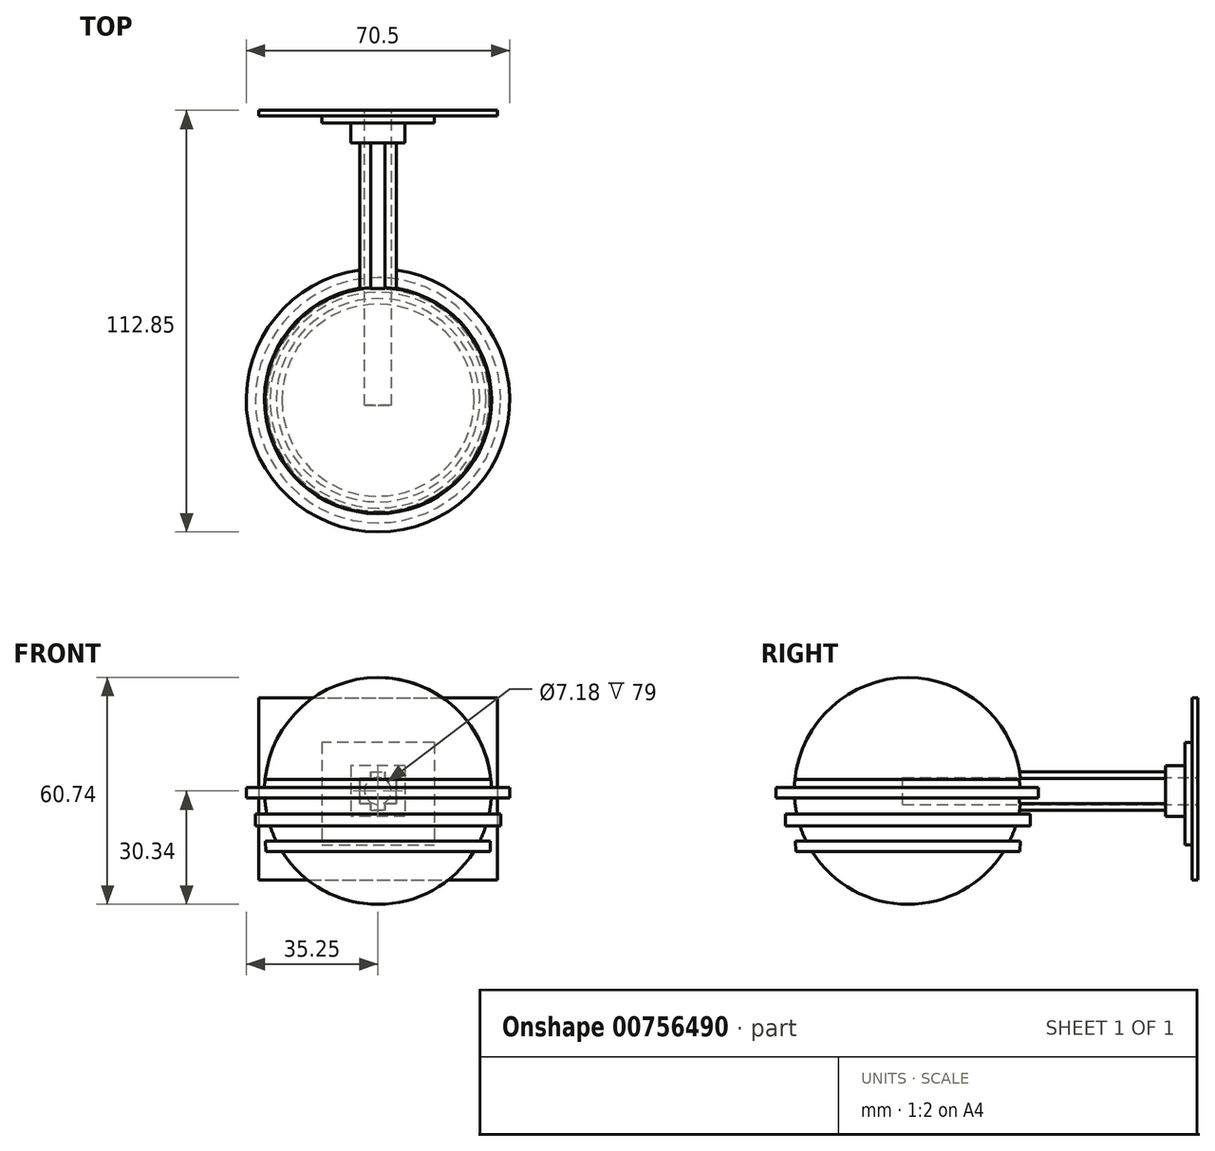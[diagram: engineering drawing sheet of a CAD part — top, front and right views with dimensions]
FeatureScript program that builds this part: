
annotation { "Feature Type Name" : "Feature", "Feature Type Description" : "" }
export const myFeature = defineFeature(function(context is Context, id is Id, definition is map)
    precondition{}
    {
        {
            var Q0;
            Q0=qCreatedBy(makeId("Front.planeOp"),FACE);
            var sketch = newSketch(context, id + "F0", { "sketchPlane" : qUnion([Q0])});
            skLineSegment(sketch, "E0", {"start": v(0, 24.98) * mm, "end": v(-31.95, 24.98) * mm});
            skLineSegment(sketch, "E1", {"start": v(-31.95, 24.98) * mm, "end": v(-31.95, -23.86) * mm});
            skLineSegment(sketch, "E2", {"start": v(-31.95, -23.86) * mm, "end": v(0, -23.86) * mm});
            skLineSegment(sketch, "E3.MirrorCS", {"start": v(0, 24.98) * mm, "end": v(31.95, 24.98) * mm});
            skLineSegment(sketch, "E4.MirrorCS", {"start": v(31.95, -23.86) * mm, "end": v(0, -23.86) * mm});
            skLineSegment(sketch, "E5.MirrorCS", {"start": v(31.95, 24.98) * mm, "end": v(31.95, -23.86) * mm});
            skLineSegment(sketch, "E6.bottom", {"start": v(0, 12.97) * mm, "end": v(-15.06, 12.97) * mm});
            skLineSegment(sketch, "E6.top", {"start": v(0, -14.42) * mm, "end": v(-15.06, -14.42) * mm});
            skLineSegment(sketch, "E6.right", {"start": v(-15.06, 12.97) * mm, "end": v(-15.06, -14.42) * mm});
            skLineSegment(sketch, "E7", {"start": v(0.36, 6.77) * mm, "end": v(-7.26, 6.77) * mm});
            skLineSegment(sketch, "E8", {"start": v(-7.26, 6.77) * mm, "end": v(-7.26, -6.8) * mm});
            skLineSegment(sketch, "E9", {"start": v(-7.26, -6.8) * mm, "end": v(0, -6.8) * mm});
            skLineSegment(sketch, "E10.MirrorCS", {"start": v(0, -14.42) * mm, "end": v(15.06, -14.42) * mm});
            skLineSegment(sketch, "E11.MirrorCS", {"start": v(15.06, 12.97) * mm, "end": v(15.06, -14.42) * mm});
            skLineSegment(sketch, "E12.MirrorCS", {"start": v(0, 12.97) * mm, "end": v(15.06, 12.97) * mm});
            skLineSegment(sketch, "E13.MirrorCS", {"start": v(-0.36, 6.77) * mm, "end": v(7.26, 6.77) * mm});
            skLineSegment(sketch, "E14.MirrorCS", {"start": v(7.26, 6.77) * mm, "end": v(7.26, -6.8) * mm});
            skLineSegment(sketch, "E15.MirrorCS", {"start": v(7.26, -6.8) * mm, "end": v(0, -6.8) * mm});
            skLineSegment(sketch, "E16.bottom", {"start": v(-1.88, 3.37) * mm, "end": v(-4.91, 3.37) * mm});
            skLineSegment(sketch, "E16.top", {"start": v(-1.88, -3.37) * mm, "end": v(-4.91, -3.37) * mm});
            skLineSegment(sketch, "E16.right", {"start": v(-4.91, 3.37) * mm, "end": v(-4.91, -3.37) * mm});
            skLineSegment(sketch, "E17.MirrorCS", {"start": v(1.88, 3.37) * mm, "end": v(4.91, 3.37) * mm});
            skLineSegment(sketch, "E18.MirrorCS", {"start": v(4.91, 3.37) * mm, "end": v(4.91, -3.37) * mm});
            skLineSegment(sketch, "E19.MirrorCS", {"start": v(1.88, -3.37) * mm, "end": v(4.91, -3.37) * mm});
            skLineSegment(sketch, "E20", {"start": v(-1.88, -3.37) * mm, "end": v(-1.88, -5.2) * mm});
            skLineSegment(sketch, "E21", {"start": v(-1.88, -5.2) * mm, "end": v(0, -5.2) * mm});
            skLineSegment(sketch, "E22.MirrorCS", {"start": v(-1.88, 3.37) * mm, "end": v(-1.88, 5.2) * mm});
            skLineSegment(sketch, "E23.MirrorCS", {"start": v(-1.88, 5.2) * mm, "end": v(0, 5.2) * mm});
            skLineSegment(sketch, "E24.MirrorCS", {"start": v(1.88, -3.37) * mm, "end": v(1.88, -5.2) * mm});
            skLineSegment(sketch, "E25.MirrorCS", {"start": v(1.88, -5.2) * mm, "end": v(0, -5.2) * mm});
            skLineSegment(sketch, "E26.MirrorCS", {"start": v(1.88, 3.37) * mm, "end": v(1.88, 5.2) * mm});
            skLineSegment(sketch, "E27.MirrorCS", {"start": v(1.88, 5.2) * mm, "end": v(0, 5.2) * mm});
            skSolve(sketch);
        }
        {
            var Q0;
            Q0=makeQuery(id+"F0.imprint","IMPRINT",FACE,{"disambiguationData":[TD([[makeQuery(id+"F0.imprint","IMPRINT",EDGE,{"derivedFrom":sQuery(id+"F0.wireOp",EDGE,"E7")}),1.0]])]});
            extrude(context, id + "F1", {"entities" : qUnion([Q0]), "depth" : 8.7 * mm, "offsetDistance" : 25 * mm});
        }
        {
            var Q0;
            Q0=makeQuery(id+"F0.imprint","IMPRINT",FACE,{"disambiguationData":[TD([[makeQuery(id+"F0.imprint","IMPRINT",EDGE,{"derivedFrom":sQuery(id+"F0.wireOp",EDGE,"E6.bottom")}),1.0]])]});
            extrude(context, id + "F2", {"entities" : qUnion([Q0]), "operationType" : NewBodyOperationType.ADD, "depth" : 3.4 * mm, "offsetDistance" : 25 * mm});
        }
        {
            var Q0;
            Q0=makeQuery(id+"F0.imprint","IMPRINT",FACE,{"disambiguationData":[TD([[makeQuery(id+"F0.imprint","IMPRINT",EDGE,{"derivedFrom":sQuery(id+"F0.wireOp",EDGE,"E16.bottom")}),1.0]])]});
            extrude(context, id + "F3", {"entities" : qUnion([Q0]), "operationType" : NewBodyOperationType.ADD, "depth" : 77.6 * mm, "offsetDistance" : 25 * mm});
        }
        {
            var Q0;
            Q0=makeQuery(id+"F3.opExtrude","CAP_FACE",FACE,{"disambiguationData":[OSD([sQuery(id+"F0.wireOp",EDGE,"E16.bottom"),sQuery(id+"F0.wireOp",EDGE,"E16.top"),sQuery(id+"F0.wireOp",EDGE,"E16.right"),sQuery(id+"F0.wireOp",EDGE,"E17.MirrorCS"),sQuery(id+"F0.wireOp",EDGE,"E18.MirrorCS"),sQuery(id+"F0.wireOp",EDGE,"E19.MirrorCS")])],"isStart":false});
            var sketch = newSketch(context, id + "F4", { "sketchPlane" : qUnion([Q0])});
            skArc(sketch, "E28", {"start": v(0, 30.4) * mm, "mid": v(-20.38, 22.55) * mm, "end": v(-30.22, 3.06) * mm});
            skPoint(sketch, "E29", {"position": v(0, -3.37) * mm});
            skLineSegment(sketch, "E30", {"start": v(0, 30.4) * mm, "end": v(0, -30.34) * mm});
            skArc(sketch, "E31.trimOffspring", {"start": v(-30.3, -1.89) * mm, "mid": v(-30.1, -4.03) * mm, "end": v(-29.74, -6.15) * mm});
            skLineSegment(sketch, "E32", {"start": v(-30.21, 3.06) * mm, "end": v(-30.22, 3.06) * mm});
            skArc(sketch, "E33", {"start": v(-30.21, 3.06) * mm, "mid": v(-30.33, 2.02) * mm, "end": v(-30.4, 0.98) * mm});
            skLineSegment(sketch, "E34", {"start": v(-30.3, -1.89) * mm, "end": v(-35.25, -1.89) * mm});
            skLineSegment(sketch, "E35", {"start": v(-35.25, -1.89) * mm, "end": v(-35.25, 0.98) * mm});
            skLineSegment(sketch, "E36", {"start": v(-35.25, 0.98) * mm, "end": v(-30.4, 0.98) * mm});
            skLineSegment(sketch, "E37", {"start": v(-29.74, -6.15) * mm, "end": v(-32.82, -6.15) * mm});
            skPoint(sketch, "E37.endSnap0", {"position": v(-32.82, 0.98) * mm});
            skLineSegment(sketch, "E38", {"start": v(-32.82, -6.15) * mm, "end": v(-32.82, -9.34) * mm});
            skLineSegment(sketch, "E39", {"start": v(-32.82, -9.34) * mm, "end": v(-28.89, -9.34) * mm});
            skArc(sketch, "E40.trimOffspring", {"start": v(-28.89, -9.34) * mm, "mid": v(-28.13, -11.42) * mm, "end": v(-27.22, -13.43) * mm});
            skLineSegment(sketch, "E41", {"start": v(-27.22, -13.43) * mm, "end": v(-30.08, -13.43) * mm});
            skLineSegment(sketch, "E42", {"start": v(-30.08, -13.43) * mm, "end": v(-30.02, -16.23) * mm});
            skLineSegment(sketch, "E43", {"start": v(-30.02, -16.23) * mm, "end": v(-25.7, -16.14) * mm});
            skArc(sketch, "E44.trimOffspring", {"start": v(-25.7, -16.14) * mm, "mid": v(-14.68, -26.55) * mm, "end": v(0, -30.34) * mm});
            skSolve(sketch);
        }
        {
            var Q0;
            {var subQ2=sQuery(id+"F4.wireOp",EDGE,"E28");Q0=makeQuery(id+"F4.imprint","IMPRINT",FACE,{"disambiguationData":[TD([[makeQuery(id+"F4.imprint","IMPRINT",EDGE,{"derivedFrom":subQ2}),1.0]])]});}
            var Q1;
            {var subQ5=makeQuery(id+"F3.opExtrude","CAP_EDGE",EDGE,{"disambiguationData":[OSD([sQuery(id+"F0.wireOp",EDGE,"E16.right")])],"isStart":false});Q1=makeQuery(id+"F4.imprint","IMPRINT",FACE,{"disambiguationData":[TD([[makeQuery(id+"F4.imprint","IMPRINT",EDGE,{"derivedFrom":subQ5}),1.0]])]});}
            var Q2;
            Q2=sQuery(id+"F4.wireOp",EDGE,"E30");
            revolve(context, id + "F5", {"operationType" : NewBodyOperationType.ADD, "surfaceOperationType" : NewSurfaceOperationType.NEW, "entities" : qUnion([Q0, Q1]), "axis" : qUnion([Q2]), "revolveType" : RevolveType.FULL});
        }
        {
            var Q0;
            Q0=makeQuery(id+"F0.imprint","IMPRINT",FACE,{"disambiguationData":[TD([[makeQuery(id+"F0.imprint","IMPRINT",EDGE,{"derivedFrom":sQuery(id+"F0.wireOp",EDGE,"E0")}),1.0]])]});
            extrude(context, id + "F6", {"entities" : qUnion([Q0]), "operationType" : NewBodyOperationType.ADD, "depth" : 1.5 * mm, "offsetDistance" : 25 * mm});
        }
        {
            var Q0;
            Q0=qCreatedBy(makeId("Front.planeOp"),FACE);
            var sketch = newSketch(context, id + "F7", { "sketchPlane" : qUnion([Q0])});
            skCircle(sketch, "E45", {"center": v(0, 0) * mm, "radius": 3.6 * mm});
            skSolve(sketch);
        }
        {
            var Q0;
            Q0=makeQuery(id+"F7.imprint","IMPRINT",FACE,{"disambiguationData":[TD([[makeQuery(id+"F7.imprint","IMPRINT",EDGE,{"derivedFrom":sQuery(id+"F7.wireOp",EDGE,"E45")}),1.0]])]});
            extrude(context, id + "F8", {"entities" : qUnion([Q0]), "operationType" : NewBodyOperationType.REMOVE, "depth" : 79 * mm, "offsetDistance" : 25 * mm});
        }
    });
